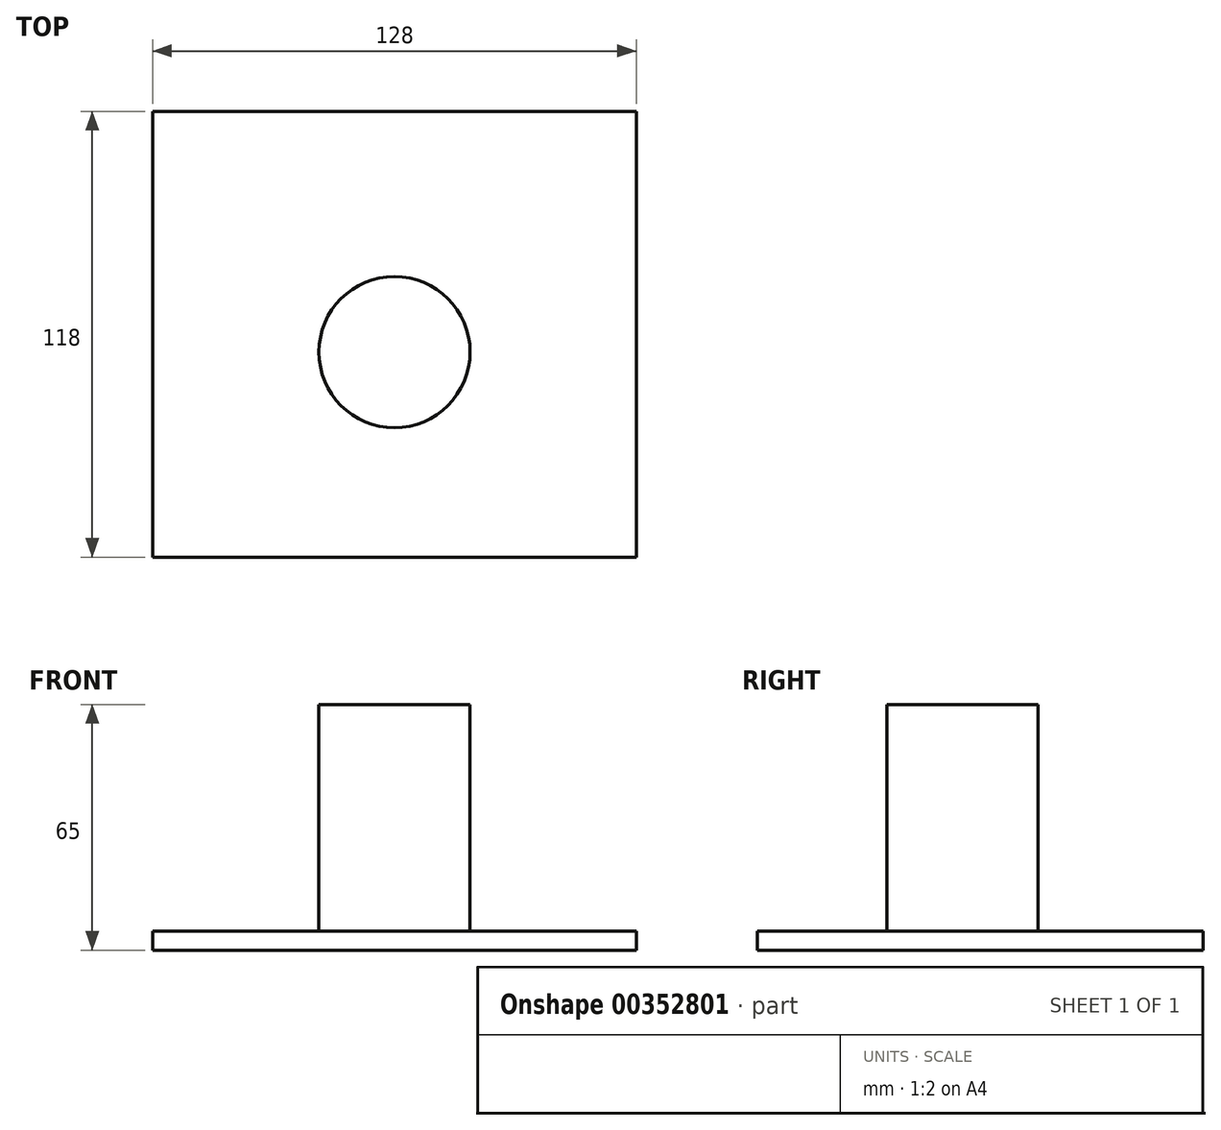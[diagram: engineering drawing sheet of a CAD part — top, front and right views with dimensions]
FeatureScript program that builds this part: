
annotation { "Feature Type Name" : "Feature", "Feature Type Description" : "" }
export const myFeature = defineFeature(function(context is Context, id is Id, definition is map)
    precondition{}
    {
        {
            var Q0;
            Q0=qCreatedBy(makeId("Top.planeOp"),FACE);
            var sketch = newSketch(context, id + "F0", { "sketchPlane" : qUnion([Q0])});
            skLineSegment(sketch, "E0.bottom", {"start": v(-64, 59) * mm, "end": v(64, 59) * mm});
            skLineSegment(sketch, "E0.top", {"start": v(-64, -59) * mm, "end": v(64, -59) * mm});
            skLineSegment(sketch, "E0.left", {"start": v(-64, 59) * mm, "end": v(-64, -59) * mm});
            skLineSegment(sketch, "E0.right", {"start": v(64, 59) * mm, "end": v(64, -59) * mm});
            skPoint(sketch, "E0.middle", {"position": v(0, 0) * mm});
            skSolve(sketch);
        }
        {
            var Q0;
            Q0=makeQuery(id+"F0.imprint","IMPRINT",FACE,{"disambiguationData":[TD([[makeQuery(id+"F0.imprint","IMPRINT",EDGE,{"derivedFrom":sQuery(id+"F0.wireOp",EDGE,"E0.bottom")}),-1.0]])]});
            extrude(context, id + "F1", {"entities" : qUnion([Q0]), "depth" : 5 * mm, "offsetDistance" : 25 * mm});
        }
        {
            var Q0;
            Q0=makeQuery(id+"F1.opExtrude","CAP_FACE",FACE,{"disambiguationData":[OSD([sQuery(id+"F0.wireOp",EDGE,"E0.bottom"),sQuery(id+"F0.wireOp",EDGE,"E0.top"),sQuery(id+"F0.wireOp",EDGE,"E0.left"),sQuery(id+"F0.wireOp",EDGE,"E0.right")])],"isStart":false});
            var sketch = newSketch(context, id + "F2", { "sketchPlane" : qUnion([Q0])});
            skSolve(sketch);
        }
        {
            var Q0;
            Q0=makeQuery(id+"F2.imprint","IMPRINT",FACE,{"disambiguationData":[TD([[makeQuery(id+"F2.imprint","IMPRINT",EDGE,{"derivedFrom":makeQuery(id+"F1.opExtrude","CAP_EDGE",EDGE,{"disambiguationData":[OSD([sQuery(id+"F0.wireOp",EDGE,"E0.bottom")])],"isStart":false})}),-1.0]])]});
            var sketch = newSketch(context, id + "F3", { "sketchPlane" : qUnion([Q0])});
            skCircle(sketch, "E1", {"center": v(0, -4.73) * mm, "radius": 20 * mm});
            skSolve(sketch);
        }
        {
            var Q0;
            Q0=makeQuery(id+"F3.imprint","IMPRINT",FACE,{"disambiguationData":[TD([[makeQuery(id+"F3.imprint","IMPRINT",EDGE,{"derivedFrom":sQuery(id+"F3.wireOp",EDGE,"E1")}),1.0]])]});
            extrude(context, id + "F4", {"entities" : qUnion([Q0]), "operationType" : NewBodyOperationType.ADD, "depth" : 60 * mm, "offsetDistance" : 25 * mm});
        }
    });
